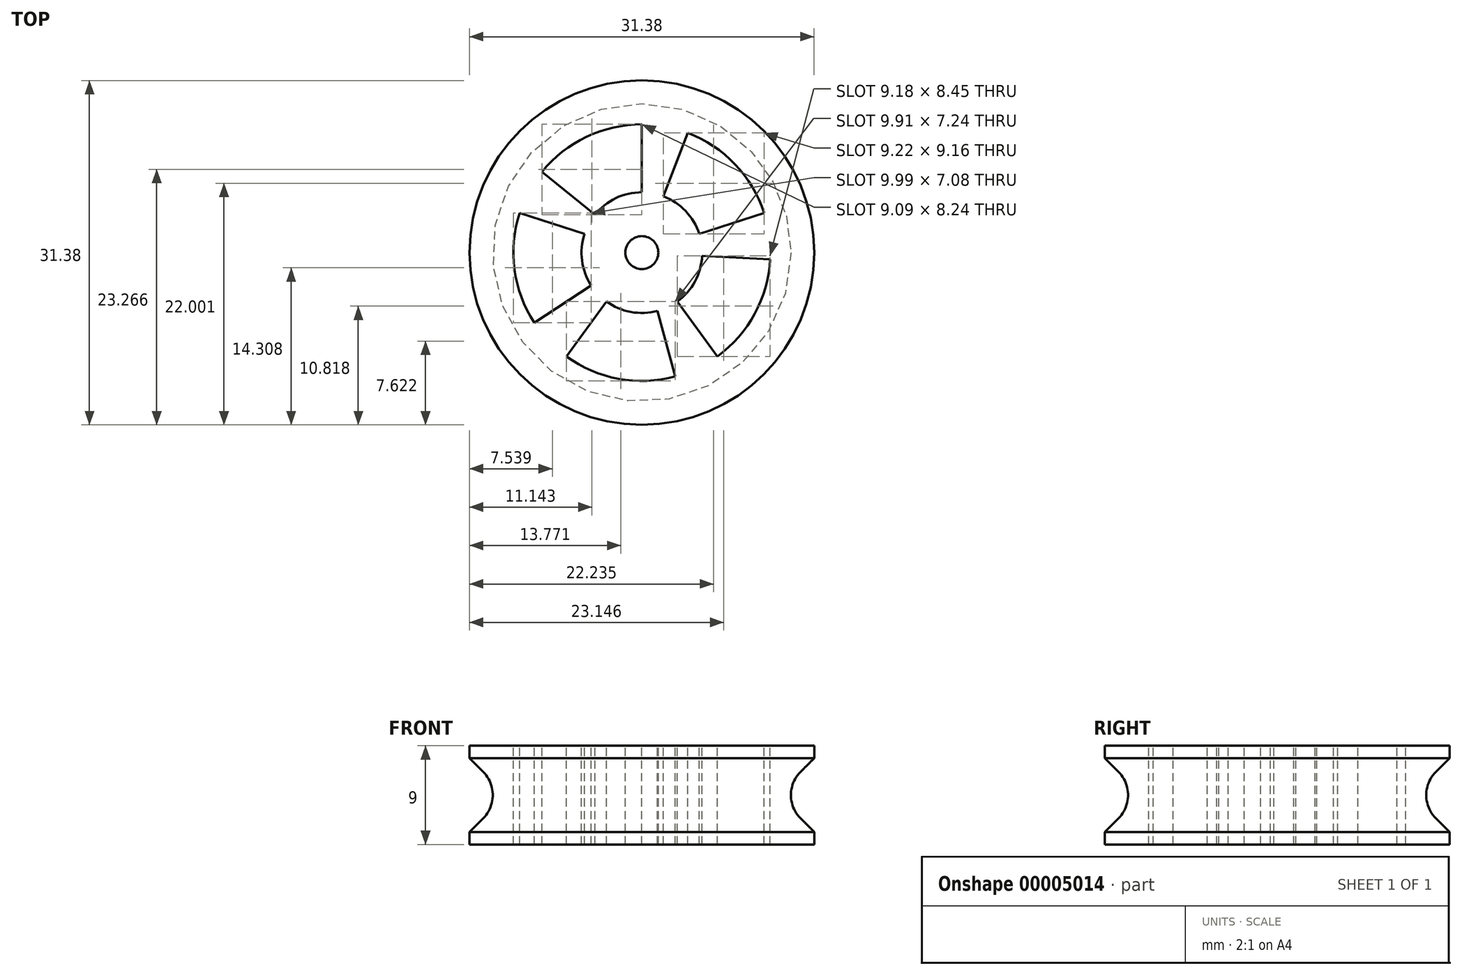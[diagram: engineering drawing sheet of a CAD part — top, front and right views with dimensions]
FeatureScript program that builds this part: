
annotation { "Feature Type Name" : "Feature", "Feature Type Description" : "" }
export const myFeature = defineFeature(function(context is Context, id is Id, definition is map)
    precondition{}
    {
        {
            var Q0;
            Q0=qCreatedBy(makeId("Front.planeOp"),FACE);
            var sketch = newSketch(context, id + "F0", { "sketchPlane" : qUnion([Q0])});
            skLineSegment(sketch, "E0", {"start": v(-14.45, 2.12) * mm, "end": v(-14.45, -2.12) * mm, "construction": true});
            skPoint(sketch, "E1", {"position": v(-14.45, 0) * mm});
            skArc(sketch, "E2", {"start": v(-14.45, -2.12) * mm, "mid": v(-13.57, 0) * mm, "end": v(-14.45, 2.12) * mm});
            skLineSegment(sketch, "E3", {"start": v(-14.45, 2.12) * mm, "end": v(-15.7, 3.36) * mm});
            skLineSegment(sketch, "E4", {"start": v(-15.7, 3.36) * mm, "end": v(-15.7, 4.5) * mm});
            skLineSegment(sketch, "E5", {"start": v(-15.7, 4.5) * mm, "end": v(0, 4.5) * mm});
            skLineSegment(sketch, "E6", {"start": v(0, 4.5) * mm, "end": v(0, 0) * mm});
            skLineSegment(sketch, "E7", {"start": v(-14.45, -2.12) * mm, "end": v(-15.7, -3.36) * mm});
            skLineSegment(sketch, "E8", {"start": v(-15.7, -3.36) * mm, "end": v(-15.7, -4.5) * mm});
            skLineSegment(sketch, "E9", {"start": v(-15.7, -4.5) * mm, "end": v(0, -4.5) * mm});
            skLineSegment(sketch, "E10", {"start": v(0, -4.5) * mm, "end": v(0, 0) * mm});
            skSolve(sketch);
        }
        {
            var Q0;
            Q0=makeQuery(id+"F0.imprint","IMPRINT",FACE,{"disambiguationData":[TD([[makeQuery(id+"F0.imprint","IMPRINT",EDGE,{"derivedFrom":sQuery(id+"F0.wireOp",EDGE,"E2")}),-1.0]])]});
            var Q1;
            Q1=sQuery(id+"F0.wireOp",EDGE,"E6");
            revolve(context, id + "F1", {"entities" : qUnion([Q0]), "axis" : qUnion([Q1]), "revolveType" : RevolveType.FULL});
        }
        {
            var Q0;
            Q0=makeQuery(id+"F1.opRevolve","SWEPT_FACE",FACE,{"disambiguationData":[OSD([sQuery(id+"F0.wireOp",EDGE,"E5")])]});
            var sketch = newSketch(context, id + "F2", { "sketchPlane" : qUnion([Q0])});
            skPoint(sketch, "E11.0", {"position": v(0, 0) * mm});
            skCircle(sketch, "E12", {"center": v(0, 0) * mm, "radius": 1.5 * mm});
            skCircle(sketch, "E13.0", {"center": v(0, 0) * mm, "radius": 11.7 * mm});
            skCircle(sketch, "E14.0", {"center": v(0, 0) * mm, "radius": 5.5 * mm});
            skLineSegment(sketch, "E15", {"start": v(0, 5.5) * mm, "end": v(0, 11.7) * mm});
            skLineSegment(sketch, "E16", {"start": v(1.97, 5.14) * mm, "end": v(4.18, 10.92) * mm});
            skLineSegment(sketch, "E17.1.0", {"start": v(-5.23, 1.7) * mm, "end": v(-11.12, 3.61) * mm});
            skLineSegment(sketch, "E17.1.2", {"start": v(-4.28, 3.46) * mm, "end": v(-9.1, 7.35) * mm});
            skLineSegment(sketch, "E17.2.0", {"start": v(-3.23, -4.45) * mm, "end": v(-6.87, -9.46) * mm});
            skLineSegment(sketch, "E17.2.2", {"start": v(-4.61, -3) * mm, "end": v(-9.8, -6.38) * mm});
            skLineSegment(sketch, "E17.3.0", {"start": v(3.23, -4.45) * mm, "end": v(6.87, -9.46) * mm});
            skLineSegment(sketch, "E17.3.2", {"start": v(1.43, -5.31) * mm, "end": v(3.04, -11.3) * mm});
            skLineSegment(sketch, "E17.4.0", {"start": v(5.23, 1.7) * mm, "end": v(11.12, 3.61) * mm});
            skLineSegment(sketch, "E17.4.2", {"start": v(5.5, -0.28) * mm, "end": v(11.68, -0.6) * mm});
            skSolve(sketch);
        }
        {
            var Q0;
            {var subQ2=sQuery(id+"F2.wireOp",EDGE,"E17.2.0");Q0=makeQuery(id+"F2.imprint","IMPRINT",FACE,{"disambiguationData":[TD([[makeQuery(id+"F2.imprint","IMPRINT",EDGE,{"derivedFrom":subQ2}),1.0]])]});}
            var Q1;
            {var subQ2=sQuery(id+"F2.wireOp",EDGE,"E17.1.0");Q1=makeQuery(id+"F2.imprint","IMPRINT",FACE,{"disambiguationData":[TD([[makeQuery(id+"F2.imprint","IMPRINT",EDGE,{"derivedFrom":subQ2}),1.0]])]});}
            var Q2;
            {var subQ2=sQuery(id+"F2.wireOp",EDGE,"E15");Q2=makeQuery(id+"F2.imprint","IMPRINT",FACE,{"disambiguationData":[TD([[makeQuery(id+"F2.imprint","IMPRINT",EDGE,{"derivedFrom":subQ2}),1.0]])]});}
            var Q3;
            {var subQ2=sQuery(id+"F2.wireOp",EDGE,"E16");Q3=makeQuery(id+"F2.imprint","IMPRINT",FACE,{"disambiguationData":[TD([[makeQuery(id+"F2.imprint","IMPRINT",EDGE,{"derivedFrom":subQ2}),-1.0]])]});}
            var Q4;
            {var subQ2=sQuery(id+"F2.wireOp",EDGE,"E17.3.0");Q4=makeQuery(id+"F2.imprint","IMPRINT",FACE,{"disambiguationData":[TD([[makeQuery(id+"F2.imprint","IMPRINT",EDGE,{"derivedFrom":subQ2}),1.0]])]});}
            var Q5;
            Q5=makeQuery(id+"F2.imprint","IMPRINT",FACE,{"disambiguationData":[TD([[makeQuery(id+"F2.imprint","IMPRINT",EDGE,{"derivedFrom":sQuery(id+"F2.wireOp",EDGE,"E12")}),1.0]])]});
            extrude(context, id + "F3", {"entities" : qUnion([Q0, Q1, Q2, Q3, Q4, Q5]), "operationType" : NewBodyOperationType.REMOVE, "endBound" : BoundingType.THROUGH_ALL, "oppositeDirection" : true, "depth" : 25 * mm});
        }
    });
